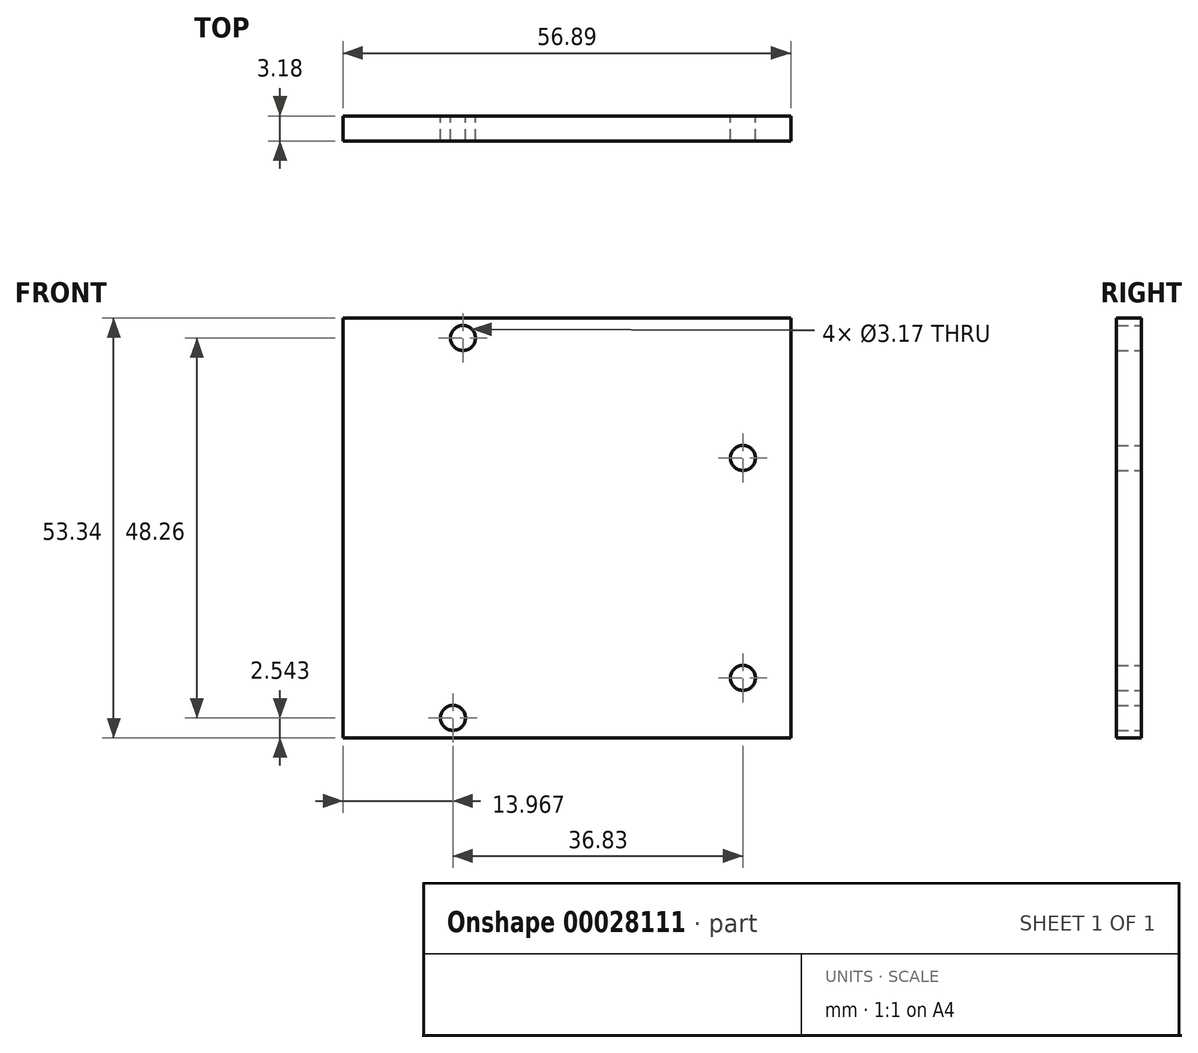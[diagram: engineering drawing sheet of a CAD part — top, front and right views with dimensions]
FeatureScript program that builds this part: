
annotation { "Feature Type Name" : "Feature", "Feature Type Description" : "" }
export const myFeature = defineFeature(function(context is Context, id is Id, definition is map)
    precondition{}
    {
        {
            var Q0;
            Q0=qCreatedBy(makeId("Front.planeOp"),FACE);
            var sketch = newSketch(context, id + "F0", { "sketchPlane" : qUnion([Q0])});
            skLineSegment(sketch, "E0.bottom", {"start": v(-28.18, 22.54) * mm, "end": v(22.62, 22.54) * mm});
            skLineSegment(sketch, "E0.top", {"start": v(-28.18, -30.8) * mm, "end": v(22.62, -30.8) * mm});
            skLineSegment(sketch, "E0.left", {"start": v(-28.18, 22.54) * mm, "end": v(-28.18, -30.8) * mm});
            skLineSegment(sketch, "E1", {"start": v(-15.8, -28.26) * mm, "end": v(-14.21, -28.26) * mm, "construction": true});
            skLineSegment(sketch, "E2", {"start": v(-14.53, 20) * mm, "end": v(-12.94, 20) * mm, "construction": true});
            skLineSegment(sketch, "E3", {"start": v(-28.18, -28.26) * mm, "end": v(-28.18, -30.8) * mm, "construction": true});
            skLineSegment(sketch, "E4", {"start": v(-28.18, 22.54) * mm, "end": v(-28.18, 20) * mm, "construction": true});
            skCircle(sketch, "E5", {"center": v(-12.94, 20) * mm, "radius": 1.59 * mm});
            skCircle(sketch, "E6", {"center": v(-14.21, -28.26) * mm, "radius": 1.59 * mm});
            skLineSegment(sketch, "E7", {"start": v(22.62, 6.35) * mm, "end": v(22.62, 4.76) * mm, "construction": true});
            skLineSegment(sketch, "E8", {"start": v(22.62, 4.76) * mm, "end": v(22.62, 3.18) * mm, "construction": true});
            skLineSegment(sketch, "E9", {"start": v(22.62, -24.76) * mm, "end": v(22.62, -23.18) * mm, "construction": true});
            skCircle(sketch, "E10", {"center": v(22.62, 4.76) * mm, "radius": 1.59 * mm});
            skCircle(sketch, "E11", {"center": v(22.62, -23.18) * mm, "radius": 1.59 * mm});
            skLineSegment(sketch, "E12.bottom", {"start": v(22.62, 22.54) * mm, "end": v(28.71, 22.54) * mm});
            skLineSegment(sketch, "E12.top", {"start": v(22.62, -30.8) * mm, "end": v(28.71, -30.8) * mm});
            skLineSegment(sketch, "E12.right", {"start": v(28.71, 22.54) * mm, "end": v(28.71, -30.8) * mm});
            skLineSegment(sketch, "E13.trimOffspring", {"start": v(22.62, 6.35) * mm, "end": v(22.62, 3.18) * mm});
            skPoint(sketch, "E12.left.end.orphan", {"position": v(22.62, 20) * mm});
            skLineSegment(sketch, "E14.trimOffspring", {"start": v(22.62, -21.59) * mm, "end": v(22.62, -24.76) * mm});
            skLineSegment(sketch, "E15.trimOffspring", {"start": v(22.62, -21.59) * mm, "end": v(22.62, -23.18) * mm, "construction": true});
            skLineSegment(sketch, "E16", {"start": v(22.62, -23.18) * mm, "end": v(22.62, 4.76) * mm, "construction": true});
            skLineSegment(sketch, "E17", {"start": v(-12.94, 20) * mm, "end": v(37.86, 20) * mm, "construction": true});
            skSolve(sketch);
        }
        {
            var Q0;
            {var subQ8=sQuery(id+"F0.wireOp",EDGE,"E0.bottom");Q0=makeQuery(id+"F0.imprint","IMPRINT",FACE,{"disambiguationData":[TD([[makeQuery(id+"F0.imprint","IMPRINT",EDGE,{"derivedFrom":subQ8}),-1.0]])]});}
            var Q1;
            {var subQ6=sQuery(id+"F0.wireOp",EDGE,"E12.bottom");Q1=makeQuery(id+"F0.imprint","IMPRINT",FACE,{"disambiguationData":[TD([[makeQuery(id+"F0.imprint","IMPRINT",EDGE,{"derivedFrom":subQ6}),-1.0]])]});}
            extrude(context, id + "F1", {"entities" : qUnion([Q0, Q1]), "depth" : 3.17 * mm});
        }
    });
